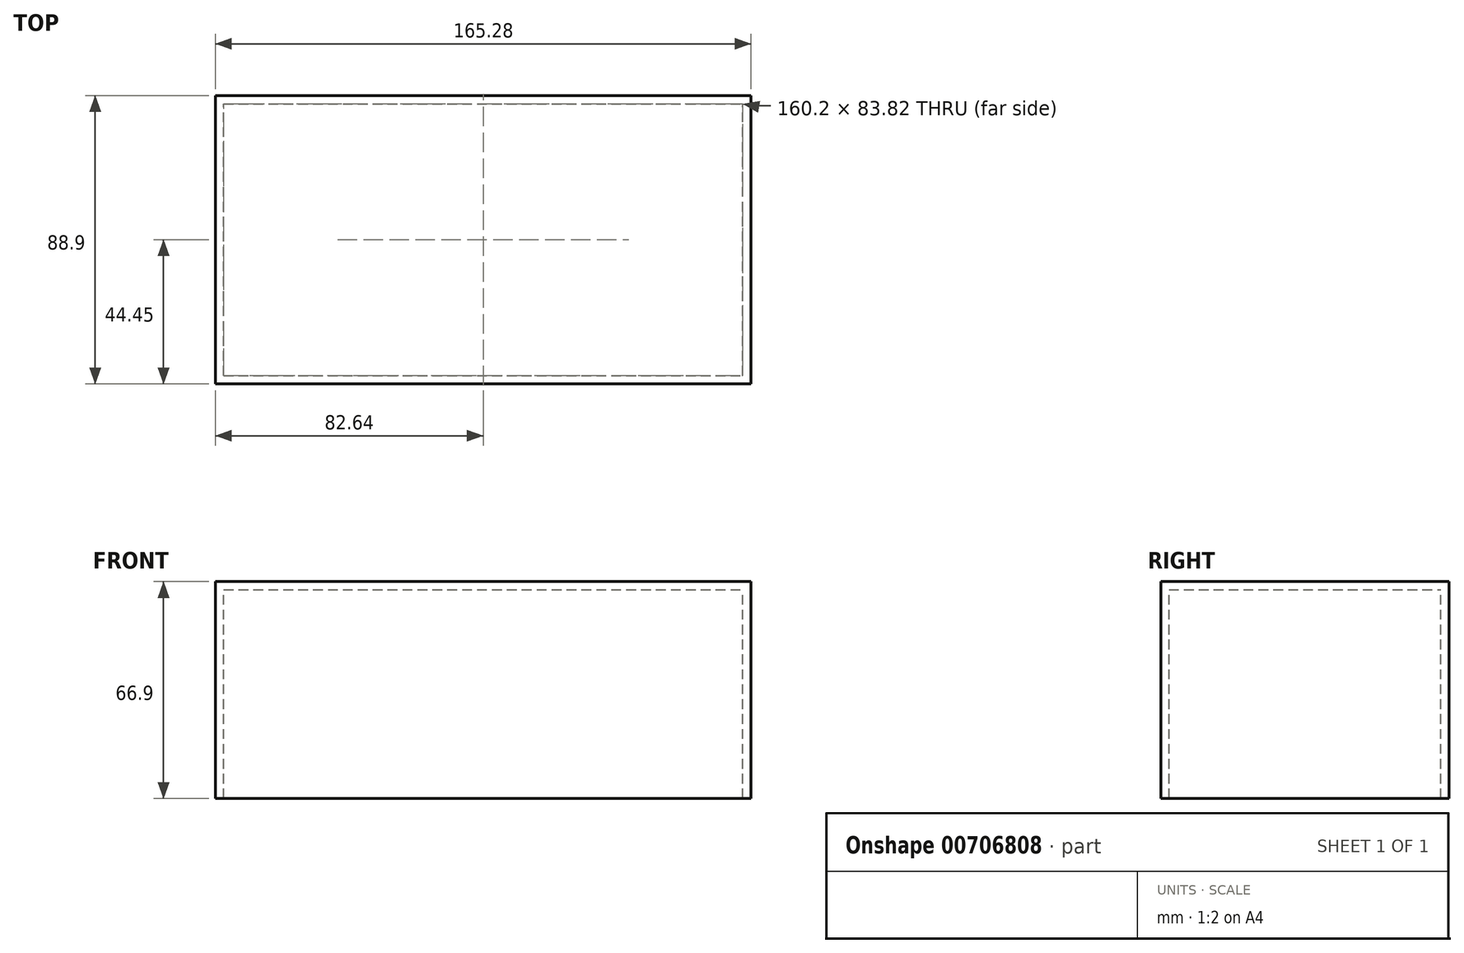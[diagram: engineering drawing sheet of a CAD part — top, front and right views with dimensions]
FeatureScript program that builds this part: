
annotation { "Feature Type Name" : "Feature", "Feature Type Description" : "" }
export const myFeature = defineFeature(function(context is Context, id is Id, definition is map)
    precondition{}
    {
        {
            var Q0;
            Q0=qCreatedBy(makeId("Front.planeOp"),FACE);
            var sketch = newSketch(context, id + "F0", { "sketchPlane" : qUnion([Q0])});
            skLineSegment(sketch, "E0.bottom", {"start": v(-82.64, -33.45) * mm, "end": v(82.64, -33.45) * mm});
            skLineSegment(sketch, "E0.top", {"start": v(-82.64, 33.45) * mm, "end": v(82.64, 33.45) * mm});
            skLineSegment(sketch, "E0.left", {"start": v(-82.64, -33.45) * mm, "end": v(-82.64, 33.45) * mm});
            skLineSegment(sketch, "E0.right", {"start": v(82.64, -33.45) * mm, "end": v(82.64, 33.45) * mm});
            skPoint(sketch, "E0.middle", {"position": v(0, 0) * mm});
            skSolve(sketch);
        }
        {
            var Q0;
            Q0=makeQuery(id+"F0.imprint","IMPRINT",FACE,{"disambiguationData":[TD([[makeQuery(id+"F0.imprint","IMPRINT",EDGE,{"derivedFrom":sQuery(id+"F0.wireOp",EDGE,"E0.bottom")}),1.0]])]});
            extrude(context, id + "F1", {"entities" : qUnion([Q0]), "depth" : 88.9 * mm, "offsetDistance" : 25.4 * mm});
        }
        {
            var Q0;
            Q0=makeQuery(id+"F1.opExtrude","SWEPT_FACE",FACE,{"disambiguationData":[OSD([sQuery(id+"F0.wireOp",EDGE,"E0.bottom")])]});
            shell(context, id + "F2", {"entities" : qUnion([Q0]), "thickness" : 2.54 * mm});
        }
    });
